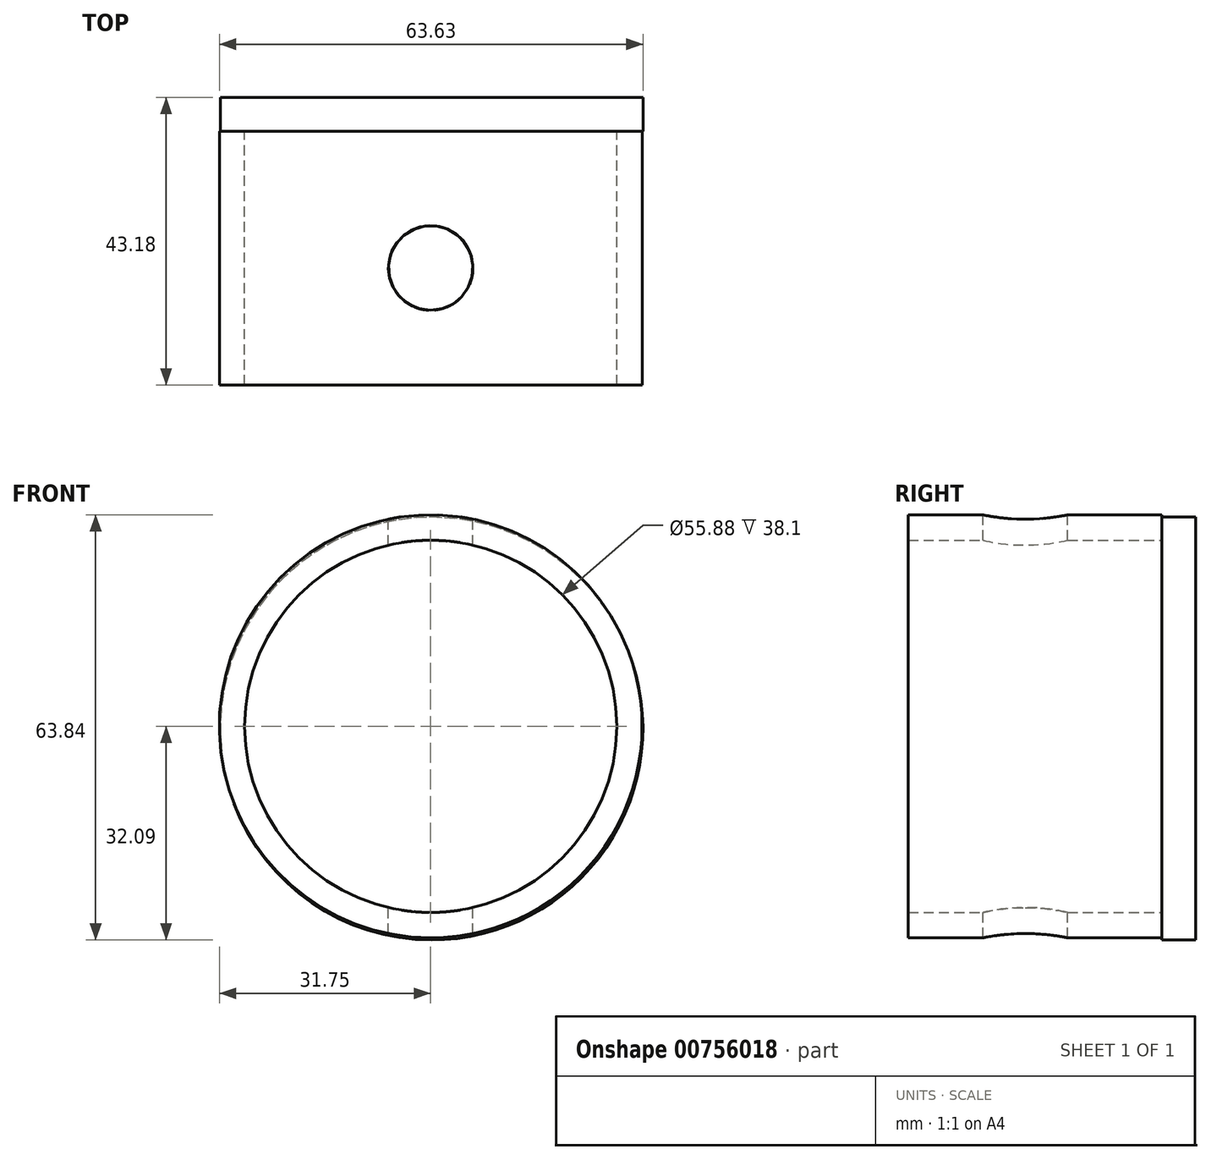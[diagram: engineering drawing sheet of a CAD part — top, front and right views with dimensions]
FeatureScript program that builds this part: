
annotation { "Feature Type Name" : "Feature", "Feature Type Description" : "" }
export const myFeature = defineFeature(function(context is Context, id is Id, definition is map)
    precondition{}
    {
        {
            var Q0;
            Q0=qCreatedBy(makeId("Front.planeOp"),FACE);
            var sketch = newSketch(context, id + "F0", { "sketchPlane" : qUnion([Q0])});
            skCircle(sketch, "E0", {"center": v(0, 0) * mm, "radius": 27.94 * mm});
            skCircle(sketch, "E1", {"center": v(0, 0) * mm, "radius": 31.75 * mm});
            skSolve(sketch);
        }
        {
            var Q0;
            Q0=makeQuery(id+"F0.imprint","IMPRINT",FACE,{"disambiguationData":[TD([[makeQuery(id+"F0.imprint","IMPRINT",EDGE,{"derivedFrom":sQuery(id+"F0.wireOp",EDGE,"E0")}),-1.0]])]});
            extrude(context, id + "F1", {"entities" : qUnion([Q0]), "depth" : 38.1 * mm, "offsetDistance" : 25.4 * mm});
        }
        {
            var Q0;
            Q0=qCreatedBy(makeId("Front.planeOp"),FACE);
            var sketch = newSketch(context, id + "F2", { "sketchPlane" : qUnion([Q0])});
            skCircle(sketch, "E2", {"center": v(0.13, -0.34) * mm, "radius": 31.75 * mm});
            skSolve(sketch);
        }
        {
            var Q0;
            Q0=makeQuery(id+"F2.imprint","IMPRINT",FACE,{"disambiguationData":[TD([[makeQuery(id+"F2.imprint","IMPRINT",EDGE,{"derivedFrom":sQuery(id+"F2.wireOp",EDGE,"E2")}),1.0]])]});
            extrude(context, id + "F3", {"entities" : qUnion([Q0]), "operationType" : NewBodyOperationType.ADD, "oppositeDirection" : true, "depth" : 5.08 * mm, "offsetDistance" : 25.4 * mm});
        }
        {
            var Q0;
            Q0=qCreatedBy(makeId("Top.planeOp"),FACE);
            var sketch = newSketch(context, id + "F4", { "sketchPlane" : qUnion([Q0])});
            skCircle(sketch, "E3", {"center": v(0, -20.53) * mm, "radius": 6.35 * mm});
            skSolve(sketch);
        }
        {
            var Q0;
            Q0=makeQuery(id+"F4.imprint","IMPRINT",FACE,{"disambiguationData":[TD([[makeQuery(id+"F4.imprint","IMPRINT",EDGE,{"derivedFrom":sQuery(id+"F4.wireOp",EDGE,"E3")}),1.0]])]});
            extrude(context, id + "F5", {"entities" : qUnion([Q0]), "operationType" : NewBodyOperationType.REMOVE, "oppositeDirection" : true, "depth" : 123.95 * mm, "offsetDistance" : 25.4 * mm, "symmetric" : true});
        }
    });
